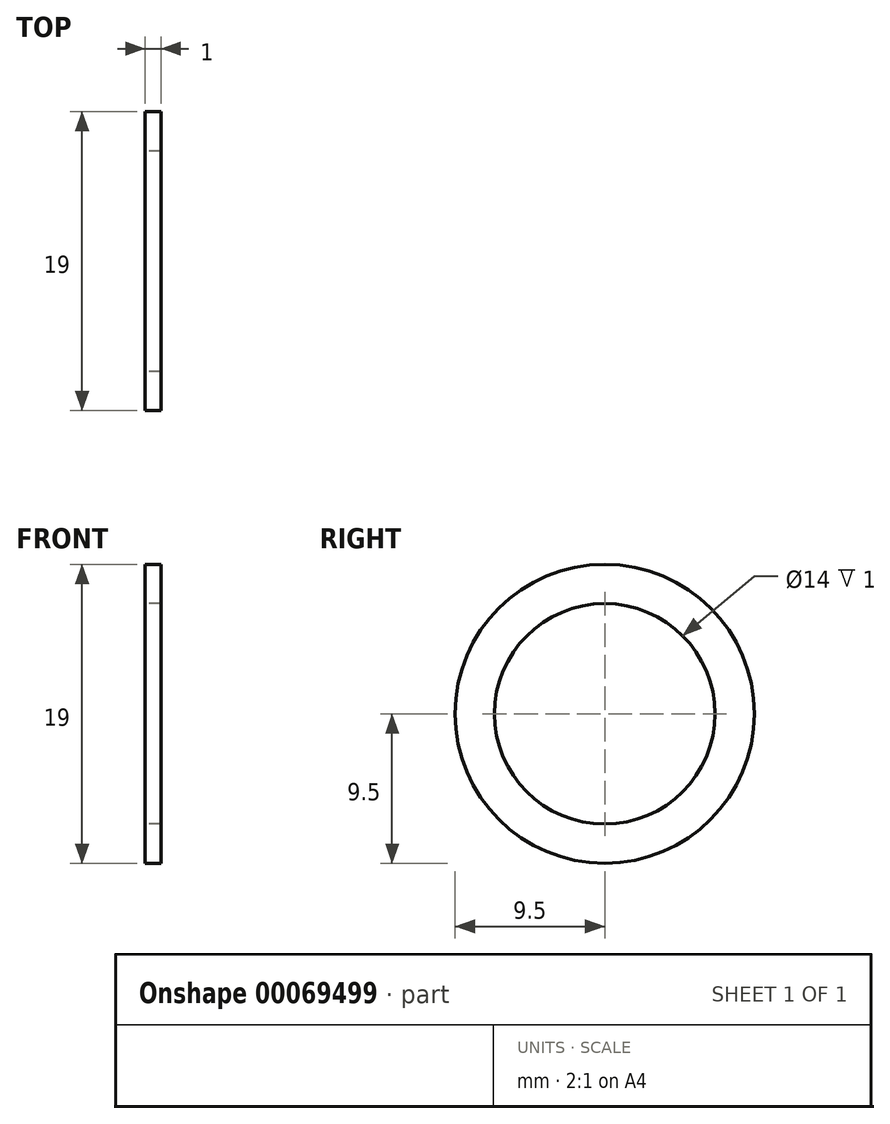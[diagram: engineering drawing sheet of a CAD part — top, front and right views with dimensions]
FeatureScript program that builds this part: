
annotation { "Feature Type Name" : "Feature", "Feature Type Description" : "" }
export const myFeature = defineFeature(function(context is Context, id is Id, definition is map)
    precondition{}
    {
        {
            var Q0;
            Q0=qCreatedBy(makeId("Right.planeOp"),FACE);
            var sketch = newSketch(context, id + "F0", { "sketchPlane" : qUnion([Q0])});
            skCircle(sketch, "E0", {"center": v(0, 0) * mm, "radius": 7 * mm});
            skCircle(sketch, "E1", {"center": v(0, 0) * mm, "radius": 9.5 * mm});
            skSolve(sketch);
        }
        {
            var Q0;
            Q0=qSketchRegion(id+"F0",true);
            extrude(context, id + "F1", {"entities" : qUnion([Q0]), "depth" : 1 * mm});
        }
    });
